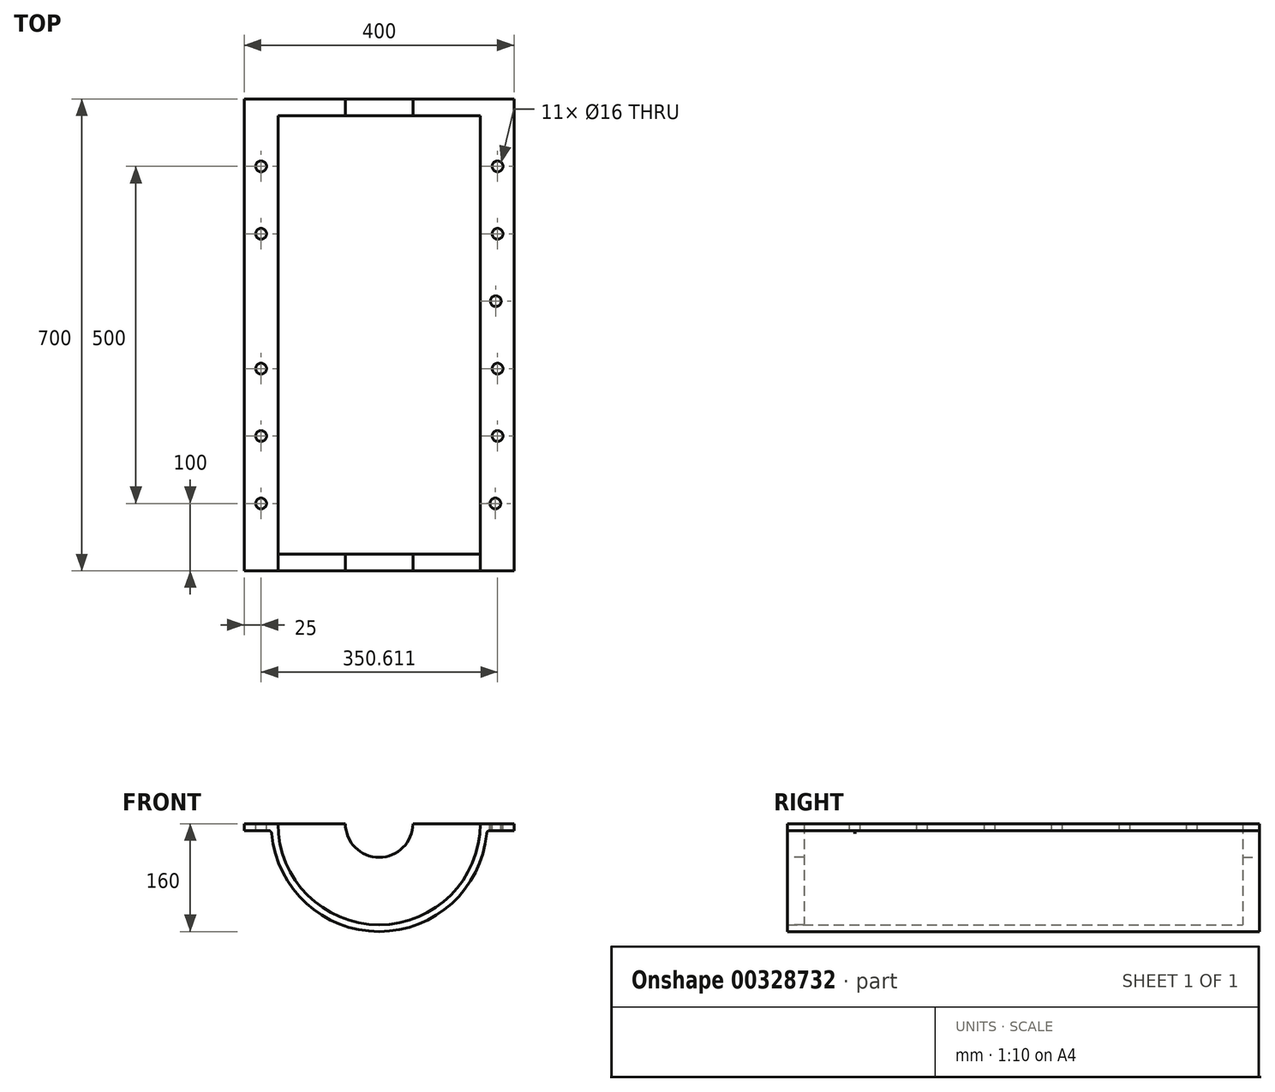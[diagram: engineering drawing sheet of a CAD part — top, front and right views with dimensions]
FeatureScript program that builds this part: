
annotation { "Feature Type Name" : "Feature", "Feature Type Description" : "" }
export const myFeature = defineFeature(function(context is Context, id is Id, definition is map)
    precondition{}
    {
        {
            var Q0;
            Q0=qCreatedBy(makeId("Front.planeOp"),FACE);
            var sketch = newSketch(context, id + "F0", { "sketchPlane" : qUnion([Q0])});
            skArc(sketch, "E0", {"start": v(-150, 0) * mm, "mid": v(0, -150) * mm, "end": v(150, 0) * mm});
            skLineSegment(sketch, "E1", {"start": v(-200, 0) * mm, "end": v(-50, 0) * mm});
            skArc(sketch, "E2", {"start": v(-50, 0) * mm, "mid": v(0, -50) * mm, "end": v(50, 0) * mm});
            skLineSegment(sketch, "E3.trimOffspring", {"start": v(50, 0) * mm, "end": v(200, 0) * mm});
            skArc(sketch, "E4.0", {"start": v(-159.68, -10.1) * mm, "mid": v(0, -160) * mm, "end": v(159.68, -10.1) * mm});
            skLineSegment(sketch, "E5", {"start": v(-200, 0) * mm, "end": v(-200, -10.1) * mm});
            skLineSegment(sketch, "E6", {"start": v(-200, -10.1) * mm, "end": v(-159.68, -10.1) * mm});
            skLineSegment(sketch, "E7", {"start": v(200, 0) * mm, "end": v(200, -10.1) * mm});
            skLineSegment(sketch, "E8", {"start": v(200, -10.1) * mm, "end": v(159.68, -10.1) * mm});
            skSolve(sketch);
        }
        {
            var Q0;
            {var subQ1=sQuery(id+"F0.wireOp",EDGE,"E0");Q0=makeQuery(id+"F0.imprint","IMPRINT",FACE,{"disambiguationData":[TD([[makeQuery(id+"F0.imprint","IMPRINT",EDGE,{"derivedFrom":subQ1}),-1.0]])]});}
            extrude(context, id + "F1", {"entities" : qUnion([Q0]), "depth" : 700 * mm});
        }
        {
            var Q0;
            Q0 = qSketchRegion(id + "F0", true);
            extrude(context, id + "F2", {"entities" : qUnion([Q0]), "operationType" : NewBodyOperationType.ADD, "depth" : 25 * mm});
        }
        {
            var Q0;
            Q0=makeQuery(id+"F1.opExtrude","CAP_FACE",FACE,{"disambiguationData":[OSD([sQuery(id+"F0.wireOp",EDGE,"E0"),sQuery(id+"F0.wireOp",EDGE,"E1"),sQuery(id+"F0.wireOp",EDGE,"E3.trimOffspring"),sQuery(id+"F0.wireOp",EDGE,"E4.0"),sQuery(id+"F0.wireOp",EDGE,"E5"),sQuery(id+"F0.wireOp",EDGE,"E6"),sQuery(id+"F0.wireOp",EDGE,"E7"),sQuery(id+"F0.wireOp",EDGE,"E8")])],"isStart":false});
            var sketch = newSketch(context, id + "F3", { "sketchPlane" : qUnion([Q0])});
            skArc(sketch, "E9", {"start": v(-50, 0) * mm, "mid": v(0, -50) * mm, "end": v(50, 0) * mm});
            skLineSegment(sketch, "E10", {"start": v(-150, 0) * mm, "end": v(-50, 0) * mm});
            skLineSegment(sketch, "E11.trimOffspring", {"start": v(50, 0) * mm, "end": v(150, 0) * mm});
            skArc(sketch, "E12", {"start": v(-150, 0) * mm, "mid": v(0, -150) * mm, "end": v(150, 0) * mm});
            skSolve(sketch);
        }
        {
            var Q0;
            Q0 = qSketchRegion(id + "F3", true);
            extrude(context, id + "F4", {"entities" : qUnion([Q0]), "oppositeDirection" : true, "depth" : 25 * mm});
        }
        {
            var Q0;
            {var subQ0=sQuery(id+"F0.wireOp",EDGE,"E1");Q0=makeQuery(id+"F2.boolean.opBoolean","MERGE",FACE,{"derivedFrom":[makeQuery(id+"F1.opExtrude","SWEPT_FACE",FACE,{"disambiguationData":[OSD([subQ0])]}),makeQuery(id+"F2.opExtrude","SWEPT_FACE",FACE,{"disambiguationData":[OSD([subQ0])]})]});}
            var sketch = newSketch(context, id + "F5", { "sketchPlane" : qUnion([Q0])});
            skCircle(sketch, "E13", {"center": v(-175, -600) * mm, "radius": 8 * mm});
            skCircle(sketch, "E14", {"center": v(-175, -500) * mm, "radius": 8 * mm});
            skCircle(sketch, "E15", {"center": v(-175, -300) * mm, "radius": 8 * mm});
            skCircle(sketch, "E16", {"center": v(-175, -200) * mm, "radius": 8 * mm});
            skCircle(sketch, "E17", {"center": v(-175, -100) * mm, "radius": 8 * mm});
            skPoint(sketch, "E18.center.orphan", {"position": v(-175, -400) * mm});
            skCircle(sketch, "E19", {"center": v(-175, -400) * mm, "radius": 8 * mm});
            skSolve(sketch);
        }
        {
            var Q0;
            {var subQ0=sQuery(id+"F0.wireOp",EDGE,"E3.trimOffspring");Q0=makeQuery(id+"F2.boolean.opBoolean","MERGE",FACE,{"derivedFrom":[makeQuery(id+"F1.opExtrude","SWEPT_FACE",FACE,{"disambiguationData":[OSD([subQ0])]}),makeQuery(id+"F2.opExtrude","SWEPT_FACE",FACE,{"disambiguationData":[OSD([subQ0])]})]});}
            var sketch = newSketch(context, id + "F6", { "sketchPlane" : qUnion([Q0])});
            skCircle(sketch, "E20", {"center": v(175.61, -100) * mm, "radius": 8 * mm});
            skCircle(sketch, "E21", {"center": v(175.61, -200) * mm, "radius": 8 * mm});
            skCircle(sketch, "E22", {"center": v(172.96, -300) * mm, "radius": 8 * mm});
            skCircle(sketch, "E23", {"center": v(175.61, -400) * mm, "radius": 8 * mm});
            skCircle(sketch, "E24", {"center": v(175.61, -500) * mm, "radius": 8 * mm});
            skCircle(sketch, "E25", {"center": v(172.3, -600) * mm, "radius": 8 * mm});
            skSolve(sketch);
        }
        {
            var Q0;
            Q0=sQuery(id+"F5.wireOp",VERTEX,"E17.center");
            var Q1;
            Q1=sQuery(id+"F6.wireOp",VERTEX,"E20.center");
            var Q2;
            Q2=sQuery(id+"F6.wireOp",VERTEX,"E21.center");
            var Q3;
            Q3=sQuery(id+"F5.wireOp",VERTEX,"E16.center");
            var Q4;
            Q4=sQuery(id+"F5.wireOp",VERTEX,"E15.center");
            var Q5;
            Q5=sQuery(id+"F6.wireOp",VERTEX,"E22.center");
            var Q6;
            Q6=sQuery(id+"F6.wireOp",VERTEX,"E23.center");
            var Q7;
            Q7=sQuery(id+"F5.wireOp",VERTEX,"E18.center.orphan");
            var Q8;
            Q8=sQuery(id+"F6.wireOp",VERTEX,"E24.center");
            var Q9;
            Q9=sQuery(id+"F5.wireOp",VERTEX,"E14.center");
            var Q10;
            Q10=sQuery(id+"F5.wireOp",VERTEX,"E13.center");
            var Q11;
            Q11=sQuery(id+"F6.wireOp",VERTEX,"E25.center");
            var Q12;
            Q12=makeQuery(id+"F1.opExtrude","SWEPT_BODY",BODY,{"disambiguationData":[OSD([sQuery(id+"F0.wireOp",EDGE,"E0"),sQuery(id+"F0.wireOp",EDGE,"E1"),sQuery(id+"F0.wireOp",EDGE,"E3.trimOffspring"),sQuery(id+"F0.wireOp",EDGE,"E4.0"),sQuery(id+"F0.wireOp",EDGE,"E5"),sQuery(id+"F0.wireOp",EDGE,"E6"),sQuery(id+"F0.wireOp",EDGE,"E7"),sQuery(id+"F0.wireOp",EDGE,"E8")])]});
            hole(context, id + "F7", {"style" : HoleStyle.SIMPLE, "endStyle" : HoleEndStyle.BLIND, "holeDiameter" : 16 * mm, "holeDepth" : 20 * mm, "tappedDepth" : 14 * mm, "tapClearance" : 3, "locations" : qUnion([Q0, Q1, Q2, Q3, Q4, Q5, Q6, Q7, Q8, Q9, Q10, Q11]), "scope" : qUnion([Q12])});
        }
        {
            var Q0;
            Q0=makeQuery(id+"F1.opExtrude","SWEPT_EDGE",EDGE,{"disambiguationData":[OSD([sQuery(id+"F0.wireOp",EDGE,"E4.0"),sQuery(id+"F0.wireOp",EDGE,"E8")])]});
            var Q1;
            Q1=makeQuery(id+"F1.opExtrude","SWEPT_EDGE",EDGE,{"disambiguationData":[OSD([sQuery(id+"F0.wireOp",EDGE,"E4.0"),sQuery(id+"F0.wireOp",EDGE,"E6")])]});
            fillet(context, id + "F8", {"entities" : qUnion([Q0, Q1]), "radius" : 5 * mm, "tangentPropagation" : true, "allowEdgeOverflow" : false});
        }
    });
